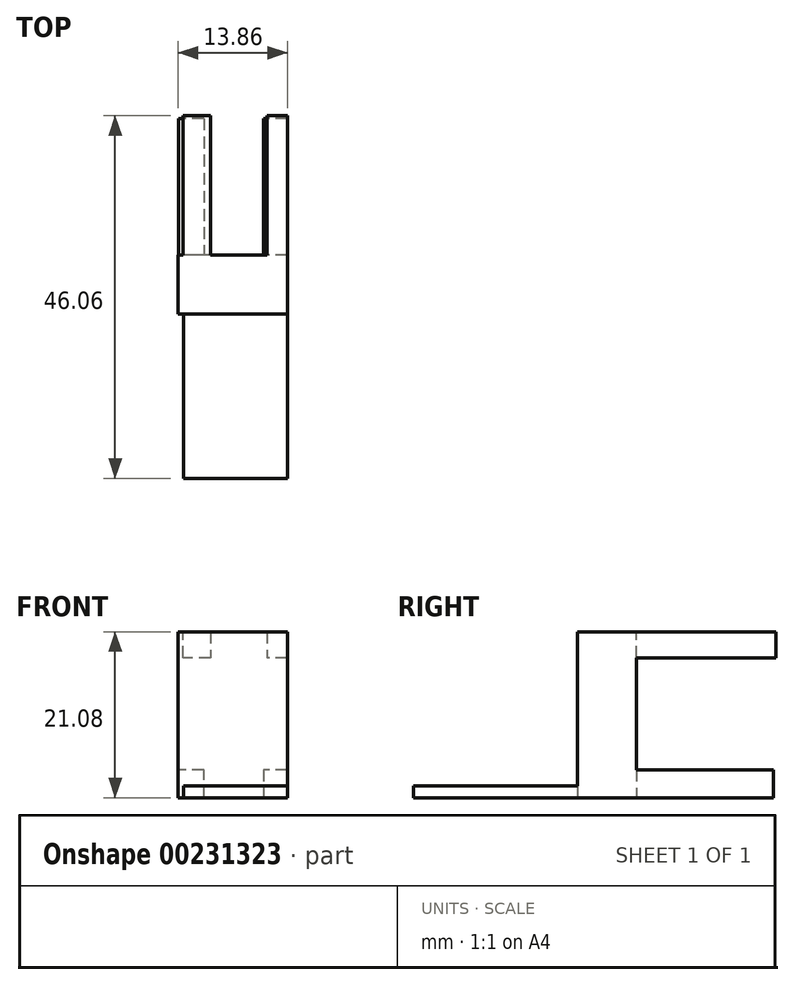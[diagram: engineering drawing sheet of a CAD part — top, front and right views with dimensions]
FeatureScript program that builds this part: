
annotation { "Feature Type Name" : "Feature", "Feature Type Description" : "" }
export const myFeature = defineFeature(function(context is Context, id is Id, definition is map)
    precondition{}
    {
        {
            var Q0;
            Q0=qCreatedBy(makeId("Top.planeOp"),FACE);
            var sketch = newSketch(context, id + "F0", { "sketchPlane" : qUnion([Q0])});
            skLineSegment(sketch, "E0", {"start": v(0, 0) * mm, "end": v(0, 24.85) * mm});
            skLineSegment(sketch, "E1", {"start": v(0, 24.85) * mm, "end": v(0, 0) * mm});
            skLineSegment(sketch, "E2", {"start": v(-13.8, 0) * mm, "end": v(-13.8, 24.85) * mm});
            skLineSegment(sketch, "E3", {"start": v(-13.8, 24.85) * mm, "end": v(-13.8, 0) * mm});
            skLineSegment(sketch, "E4", {"start": v(-3.05, 7.6) * mm, "end": v(-3.05, 24.85) * mm});
            skLineSegment(sketch, "E5", {"start": v(-3.05, 24.85) * mm, "end": v(-3.05, 7.6) * mm});
            skLineSegment(sketch, "E6", {"start": v(-10.6, 7.6) * mm, "end": v(-10.6, 24.85) * mm});
            skLineSegment(sketch, "E7", {"start": v(-10.6, 24.85) * mm, "end": v(-10.6, 7.6) * mm});
            skLineSegment(sketch, "E8", {"start": v(-10.6, 0) * mm, "end": v(-13.8, 0) * mm});
            skLineSegment(sketch, "E9", {"start": v(-10.6, 7.6) * mm, "end": v(-10.6, 0) * mm});
            skLineSegment(sketch, "E10", {"start": v(-10.6, 24.85) * mm, "end": v(-13.8, 24.85) * mm});
            skLineSegment(sketch, "E11", {"start": v(-3.05, 7.6) * mm, "end": v(-3.05, 0) * mm});
            skLineSegment(sketch, "E12", {"start": v(-3.05, 0) * mm, "end": v(0, 0) * mm});
            skLineSegment(sketch, "E13", {"start": v(0, 24.85) * mm, "end": v(-3.05, 24.85) * mm});
            skSolve(sketch);
        }
        {
            var Q0;
            Q0=qCreatedBy(makeId("Top.planeOp"),FACE);
            var sketch = newSketch(context, id + "F1", { "sketchPlane" : qUnion([Q0])});
            skLineSegment(sketch, "E14.bottom", {"start": v(0, 0) * mm, "end": v(-13.86, 0) * mm});
            skLineSegment(sketch, "E14.top", {"start": v(0, 7.48) * mm, "end": v(-13.86, 7.48) * mm});
            skLineSegment(sketch, "E14.left", {"start": v(0, 0) * mm, "end": v(0, 7.48) * mm});
            skLineSegment(sketch, "E14.right", {"start": v(-13.86, 0) * mm, "end": v(-13.86, 7.48) * mm});
            skSolve(sketch);
        }
        {
            var Q0;
            Q0 = qSketchRegion(id + "F1", true);
            extrude(context, id + "F2", {"entities" : qUnion([Q0]), "depth" : 21.08 * mm});
        }
        {
            var Q0;
            Q0 = qSketchRegion(id + "F0", true);
            extrude(context, id + "F3", {"entities" : qUnion([Q0]), "operationType" : NewBodyOperationType.ADD, "depth" : 3.56 * mm});
        }
        {
            var Q0;
            Q0=makeQuery(id+"F2.opExtrude","CAP_FACE",FACE,{"disambiguationData":[OSD([sQuery(id+"F1.wireOp",EDGE,"E14.bottom"),sQuery(id+"F1.wireOp",EDGE,"E14.top"),sQuery(id+"F1.wireOp",EDGE,"E14.left"),sQuery(id+"F1.wireOp",EDGE,"E14.right")])],"isStart":false});
            cPlane(context, id + "F4", {"entities" : qUnion([Q0]), "cplaneType" : CPlaneType.OFFSET, "offset" : 0 * mm, "width" : 152.4 * mm, "height" : 152.4 * mm});
        }
        {
            var Q0;
            Q0=qCreatedBy(id+"F4.planeOp",FACE);
            var sketch = newSketch(context, id + "F5", { "sketchPlane" : qUnion([Q0])});
            skPoint(sketch, "E15", {"position": v(-13.28, 0) * mm});
            skPoint(sketch, "E16", {"position": v(-13.28, 7.09) * mm});
            skPoint(sketch, "E17", {"position": v(0, 6.62) * mm});
            skPoint(sketch, "E18", {"position": v(0, 0) * mm});
            skLineSegment(sketch, "E19", {"start": v(0, 6.62) * mm, "end": v(0, 25.2) * mm});
            skLineSegment(sketch, "E20", {"start": v(0, 25.2) * mm, "end": v(-2.56, 25.2) * mm});
            skLineSegment(sketch, "E21", {"start": v(-2.56, 25.2) * mm, "end": v(-2.56, 6.62) * mm});
            skLineSegment(sketch, "E22", {"start": v(-2.56, 6.62) * mm, "end": v(0, 6.62) * mm});
            skLineSegment(sketch, "E23", {"start": v(-13.28, 7.09) * mm, "end": v(-13.28, 25.2) * mm});
            skLineSegment(sketch, "E24", {"start": v(-13.28, 25.2) * mm, "end": v(-9.75, 25.2) * mm});
            skLineSegment(sketch, "E25", {"start": v(-9.75, 25.2) * mm, "end": v(-9.75, 7.09) * mm});
            skLineSegment(sketch, "E26", {"start": v(-9.75, 7.09) * mm, "end": v(-13.28, 7.09) * mm});
            skLineSegment(sketch, "E27", {"start": v(-13.28, 7.09) * mm, "end": v(-9.75, 7.09) * mm});
            skLineSegment(sketch, "E28", {"start": v(0, 6.62) * mm, "end": v(-2.56, 6.62) * mm});
            skSolve(sketch);
        }
        {
            var Q0;
            Q0=makeQuery(id+"F5.imprint","IMPRINT",FACE,{"disambiguationData":[TD([[makeQuery(id+"F5.imprint","IMPRINT",EDGE,{"derivedFrom":sQuery(id+"F5.wireOp",EDGE,"E19")}),1.0]])]});
            var Q1;
            Q1=makeQuery(id+"F5.imprint","IMPRINT",FACE,{"disambiguationData":[TD([[makeQuery(id+"F5.imprint","IMPRINT",EDGE,{"derivedFrom":sQuery(id+"F5.wireOp",EDGE,"E23")}),-1.0]])]});
            extrude(context, id + "F6", {"entities" : qUnion([Q0, Q1]), "operationType" : NewBodyOperationType.ADD, "oppositeDirection" : true, "depth" : 3.3 * mm});
        }
        {
            var Q0;
            Q0=qCreatedBy(makeId("Top.planeOp"),FACE);
            var sketch = newSketch(context, id + "F7", { "sketchPlane" : qUnion([Q0])});
            skLineSegment(sketch, "E29.top", {"start": v(0, -20.86) * mm, "end": v(-13.19, -20.86) * mm});
            skLineSegment(sketch, "E29.left", {"start": v(0, 0) * mm, "end": v(0, -20.86) * mm});
            skLineSegment(sketch, "E29.right", {"start": v(-13.19, 0) * mm, "end": v(-13.19, -20.86) * mm});
            skLineSegment(sketch, "E30", {"start": v(-6.6, -20.86) * mm, "end": v(-9.16, -20.86) * mm});
            skPoint(sketch, "E31.end.orphan", {"position": v(-6.6, 0) * mm});
            skLineSegment(sketch, "E32", {"start": v(-13.19, 0) * mm, "end": v(0, 0) * mm});
            skSolve(sketch);
        }
        {
            var Q0;
            Q0 = qSketchRegion(id + "F7", true);
            extrude(context, id + "F8", {"entities" : qUnion([Q0]), "operationType" : NewBodyOperationType.ADD, "depth" : 1.52 * mm});
        }
    });
